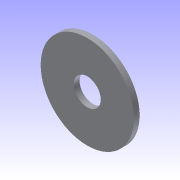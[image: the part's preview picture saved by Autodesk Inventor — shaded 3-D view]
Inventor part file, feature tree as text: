
AUTODESK INVENTOR PART (.ipt)
format: ipt  version: 2011 (Build 150239000, 239)  size: 67,072 bytes
history: native  units: in
note: dims shown in document units (in); Inventor stores cm internally (conversion verified against a paired STEP export)
features: extrude x1, sketch x1
ambient origin geometry x8: Origin, YZ Plane, XZ Plane, XY Plane, X Axis, Y Axis, Z Axis, Center Point
bodies: Solid1 (feature_tree)
feature tree (2):
  extrude  "Extrusion1"  Depth=1.005in
  sketch  "Sketch1"  dims[d0=0.29in d1=1.005in d2=0.062in d3=0.0in]
